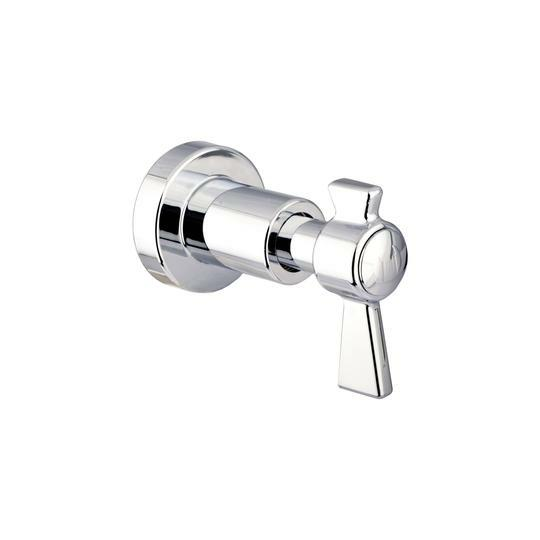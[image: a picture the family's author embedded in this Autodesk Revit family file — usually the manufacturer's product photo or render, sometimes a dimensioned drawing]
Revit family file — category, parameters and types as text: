
# Revit family: 01-1733-11-REGISTRO DUCHA HELIX PALA
name_source: partatom
category: Aparatos sanitarios
revit_build: Autodesk Revit 2018 (Build: 20170223_1515(x64)
units: mm (PartAtom-declared; Revit-internal decimal feet)

## family parameters
Anfitrión = Cara
Compartido = No
Corte con vacíos al cargar = No
Cota de conector redondo = Diámetro de uso
Número OmniClass = 23.31.11.00
Punto de cálculo de habitación = No
Tipo de pieza = Normal

## types (1)
- 01-1733-11
    Alto = 66 mm  [stored 0.216535 ft]
    Ancho = 60 mm  [stored 0.19685 ft]
    Conexión AC = Sí
    Conexión AF = Sí
    Conexión de residuos = No
    Conexión de ventilación = No
    Descripción = Registro ducha
    Elevación por defecto = 0 mm  [stored 0 ft]
    Fabricante = Gricol
    Imagen de tipo = <Ninguno>
    Link Ficha Tecnica = http://infotecnica.gricol.com
    Modelo = 01-1733-11
    Plastico ABS Cromado = Plastico ABS Cromado
    Product Name = REGISTRO DUCHA COLECCIÓN HELIX PALA
    Profundidad = 85 mm  [stored 0.278871 ft]
    URL = https://www.gricol.com

note: [stored X ft] marks values corroborated as IEEE doubles in the binary element streams (Revit-internal decimal feet)

## geometry (parser evidence)
native form markers: Blend x4, Sweep x10
no freeform markers — native parametric forms only
